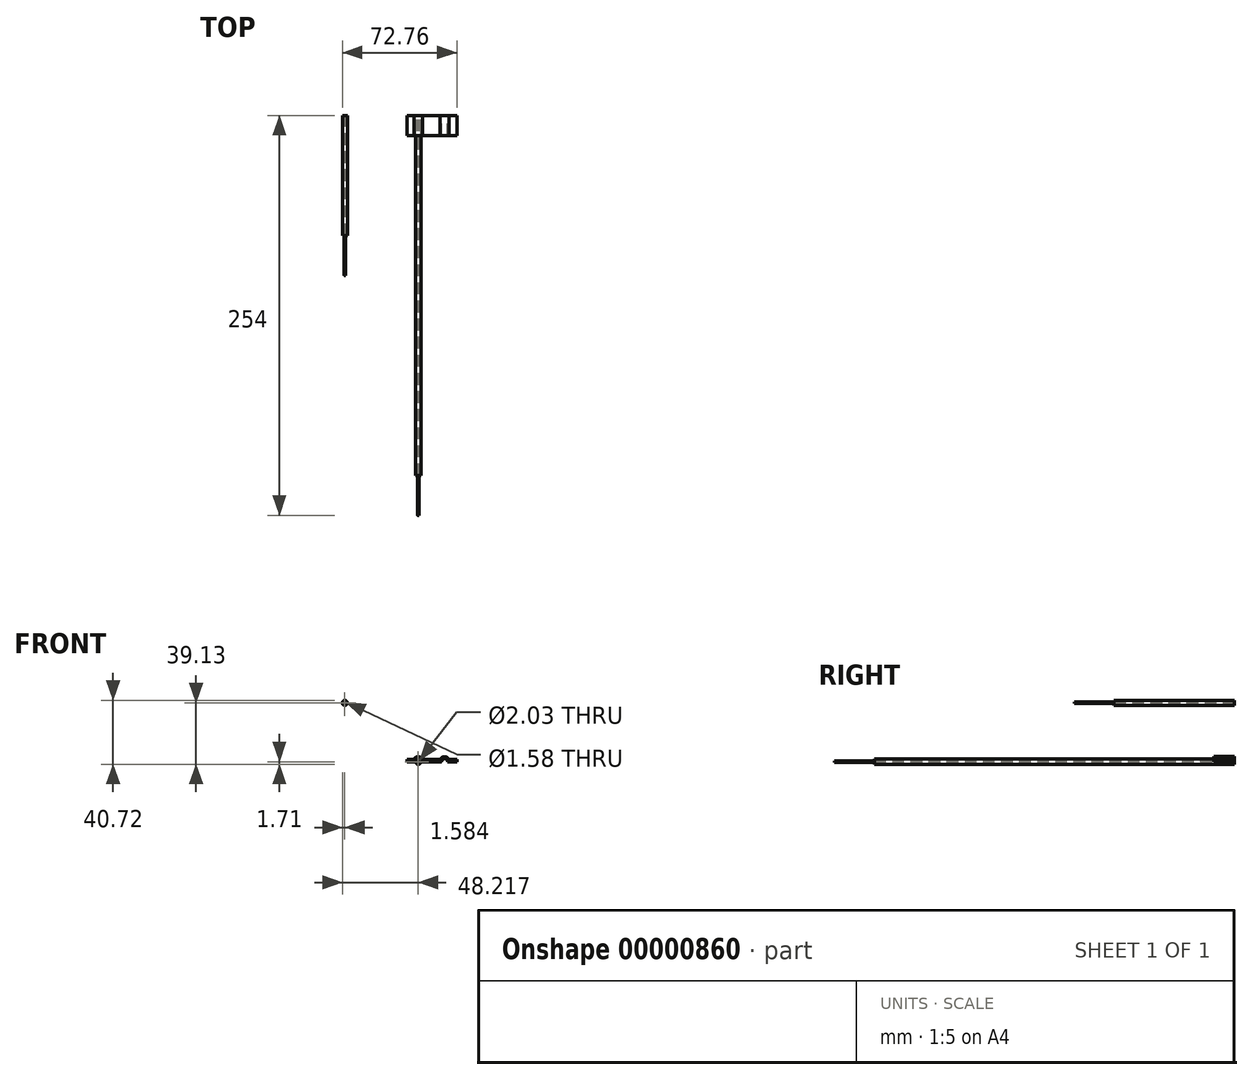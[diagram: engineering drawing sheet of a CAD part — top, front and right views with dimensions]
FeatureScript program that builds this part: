
annotation { "Feature Type Name" : "Feature", "Feature Type Description" : "" }
export const myFeature = defineFeature(function(context is Context, id is Id, definition is map)
    precondition{}
    {
        {
            var Q0;
            Q0=qCreatedBy(makeId("Front.planeOp"),FACE);
            var sketch = newSketch(context, id + "F0", { "sketchPlane" : qUnion([Q0])});
            skCircle(sketch, "E0", {"center": v(-39.43, 37.42) * mm, "radius": 1.59 * mm});
            skCircle(sketch, "E1", {"center": v(-39.43, 37.42) * mm, "radius": 0.79 * mm});
            skSolve(sketch);
        }
        {
            var Q0;
            Q0 = qSketchRegion(id + "F0", true);
            extrude(context, id + "F1", {"entities" : qUnion([Q0]), "depth" : 76.2 * mm});
        }
        {
            var Q0;
            Q0=qCreatedBy(makeId("Front.planeOp"),FACE);
            var sketch = newSketch(context, id + "F2", { "sketchPlane" : qUnion([Q0])});
            skCircle(sketch, "E2", {"center": v(-39.43, 37.4) * mm, "radius": 0.48 * mm});
            skSolve(sketch);
        }
        {
            var Q0;
            Q0 = qSketchRegion(id + "F2", true);
            extrude(context, id + "F3", {"entities" : qUnion([Q0]), "depth" : 101.6 * mm});
        }
        {
            var Q0;
            Q0=qCreatedBy(makeId("Front.planeOp"),FACE);
            var sketch = newSketch(context, id + "F4", { "sketchPlane" : qUnion([Q0])});
            skLineSegment(sketch, "E3.left", {"start": v(0, 0) * mm, "end": v(0, 1.52) * mm});
            skLineSegment(sketch, "E3.right", {"start": v(31.75, 0) * mm, "end": v(31.75, 1.52) * mm});
            skArc(sketch, "E4", {"start": v(9.04, 0) * mm, "mid": v(7.2, 1.92) * mm, "end": v(5.34, 0) * mm});
            skLineSegment(sketch, "E5", {"start": v(0, 1.52) * mm, "end": v(4.38, 1.52) * mm});
            skLineSegment(sketch, "E6", {"start": v(10, 1.52) * mm, "end": v(21.13, 1.52) * mm});
            skLineSegment(sketch, "E7", {"start": v(26.8, 1.52) * mm, "end": v(31.75, 1.52) * mm});
            skLineSegment(sketch, "E8", {"start": v(0, 0) * mm, "end": v(5.34, 0) * mm});
            skLineSegment(sketch, "E9", {"start": v(9.04, 0) * mm, "end": v(22.12, 0) * mm});
            skLineSegment(sketch, "E10", {"start": v(25.82, 0) * mm, "end": v(31.75, 0) * mm});
            skArc(sketch, "E11", {"start": v(25.82, 0) * mm, "mid": v(23.97, 1.95) * mm, "end": v(22.12, 0) * mm});
            skArc(sketch, "E12", {"start": v(10, 1.52) * mm, "mid": v(7.2, 3.2) * mm, "end": v(4.38, 1.52) * mm});
            skArc(sketch, "E13", {"start": v(26.8, 1.52) * mm, "mid": v(23.97, 3.2) * mm, "end": v(21.13, 1.52) * mm});
            skSolve(sketch);
        }
        {
            var Q0;
            Q0 = qSketchRegion(id + "F4", true);
            extrude(context, id + "F5", {"entities" : qUnion([Q0]), "depth" : 12.7 * mm});
        }
        {
            var Q0;
            Q0 = qSketchRegion(id + "F4", true);
            extrude(context, id + "F6", {"entities" : qUnion([Q0]), "operationType" : NewBodyOperationType.ADD, "depth" : 9.52 * mm});
        }
        {
            var Q0;
            Q0=qCreatedBy(makeId("Front.planeOp"),FACE);
            var sketch = newSketch(context, id + "F7", { "sketchPlane" : qUnion([Q0])});
            skCircle(sketch, "E14", {"center": v(7.2, 0) * mm, "radius": 1.71 * mm});
            skCircle(sketch, "E15", {"center": v(7.2, 0) * mm, "radius": 1.02 * mm});
            skSolve(sketch);
        }
        {
            var Q0;
            Q0=makeQuery(id+"F7.imprint","IMPRINT",FACE,{"disambiguationData":[TD([[makeQuery(id+"F7.imprint","IMPRINT",EDGE,{"derivedFrom":sQuery(id+"F7.wireOp",EDGE,"E14")}),1.0]])]});
            extrude(context, id + "F8", {"entities" : qUnion([Q0]), "depth" : 228.6 * mm});
        }
        {
            var Q0;
            Q0=qCreatedBy(makeId("Front.planeOp"),FACE);
            var sketch = newSketch(context, id + "F9", { "sketchPlane" : qUnion([Q0])});
            skCircle(sketch, "E16", {"center": v(7.2, 0) * mm, "radius": 0.5 * mm});
            skSolve(sketch);
        }
        {
            var Q0;
            Q0=makeQuery(id+"F9.imprint","IMPRINT",FACE,{"disambiguationData":[TD([[makeQuery(id+"F9.imprint","IMPRINT",EDGE,{"derivedFrom":sQuery(id+"F9.wireOp",EDGE,"E16")}),1.0]])]});
            extrude(context, id + "F10", {"entities" : qUnion([Q0]), "depth" : 254 * mm});
        }
    });
